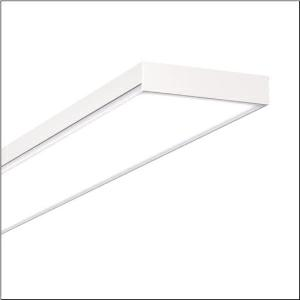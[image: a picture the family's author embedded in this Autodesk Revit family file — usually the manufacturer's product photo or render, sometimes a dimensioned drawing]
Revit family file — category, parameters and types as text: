
# Revit family: apollon_r__31_surface_51mp26wm2341w_1193
name_source: partatom
category: Lighting Fixtures
units: mm (PartAtom-declared; Revit-internal decimal feet)

## family parameters
Cut with Voids When Loaded = No
Host = Face
Light Source = No
Part Type = Normal
Room Calculation Point = No
Round Connector Dimension = Use Diameter
Shared = No

## types (1)
- Apollon® 31 Surface (1 x LED, 4400 lm, 33 W, 3000K)
    Apparent Load = 33 VA
    CIE Flux Codes = 61 87 97 97 100
    Color Rendering = 80
    Color Temperature = 3000K
    Default Elevation = 1800 mm
    Description = Apollon® 31 Surface, office luminaire, primary optical cover: micro prismatic cover, of PMMA, light emission: direct distribution, primary light characteristic: symmetric, installation type: surface-mounted, LED, rated luminous flux: 4.400lm, luminous efficacy: 133lm/W, light colour: 830, colour temperature: 3000K, control gear: ECG Multilumen, with terminal, 3-pole, mains connection: 220..240V, AC, 50/60Hz, rated input power: 33W, housing, of sheet steel, coil coated, traffic white (RAL 9016), length: 1.545mm, width: 200mm, height: 44mm, protection rating (complete): IP20, insulation class (complete): insulation class II (safety insulation), certification: CE, impact resistance: IK02, permissible operating ambient temperature: -20..+40°C, packaging unit: 1 piece
    Height = 44 mm
    Lamp = 1 x LED
    Lamp Light Flux = 4400 lm
    Lamp Power = 33 W
    Lamp count = 1
    Length = 1545 mm
    Luminous efficacy = 133 lm/W
    Manufacturer = Siteco
    ModVariant = No
    Model = 51MP26WM2341W
    Mounting Place = Ceiling
    Mounting Type = Surface mounted
    Number of Poles = 1
    OnlyDefault = Yes
    Power Factor = 1
    Product Name = Apollon® 31 Surface
    Product group = office luminaire | ceiling mounted
    ProductGroupID = 304
    Protection Class = Protection class II
    Protection Degree = IP 20
    RLX_Detail_Level = 1
    RLX_Emergency_Light_Flux = 0 lm
    RLX_Emergency_Type = 0
    RLX_Emergency_Type_DB = No
    RlxData = <blob elided: 20749 chars, md5=75b93081>
    Socket = socket
    Standby Power = 0 W
    System Light Flux = 4400 lm
    System Power = 33 W
    Type Comments = Product without accessories
    Type Image = l_1007095.jpg
    URL = http://relux.com
    VarID = ---
    Voltage = 0 V
    Weight = 0.00 kg
    Width = 200 mm  [stored 0.656168 ft]

note: [stored X ft] marks values corroborated as IEEE doubles in the binary element streams (Revit-internal decimal feet)

## geometry (parser evidence)
native form markers: Blend x4, Sweep x13
no freeform markers — native parametric forms only
